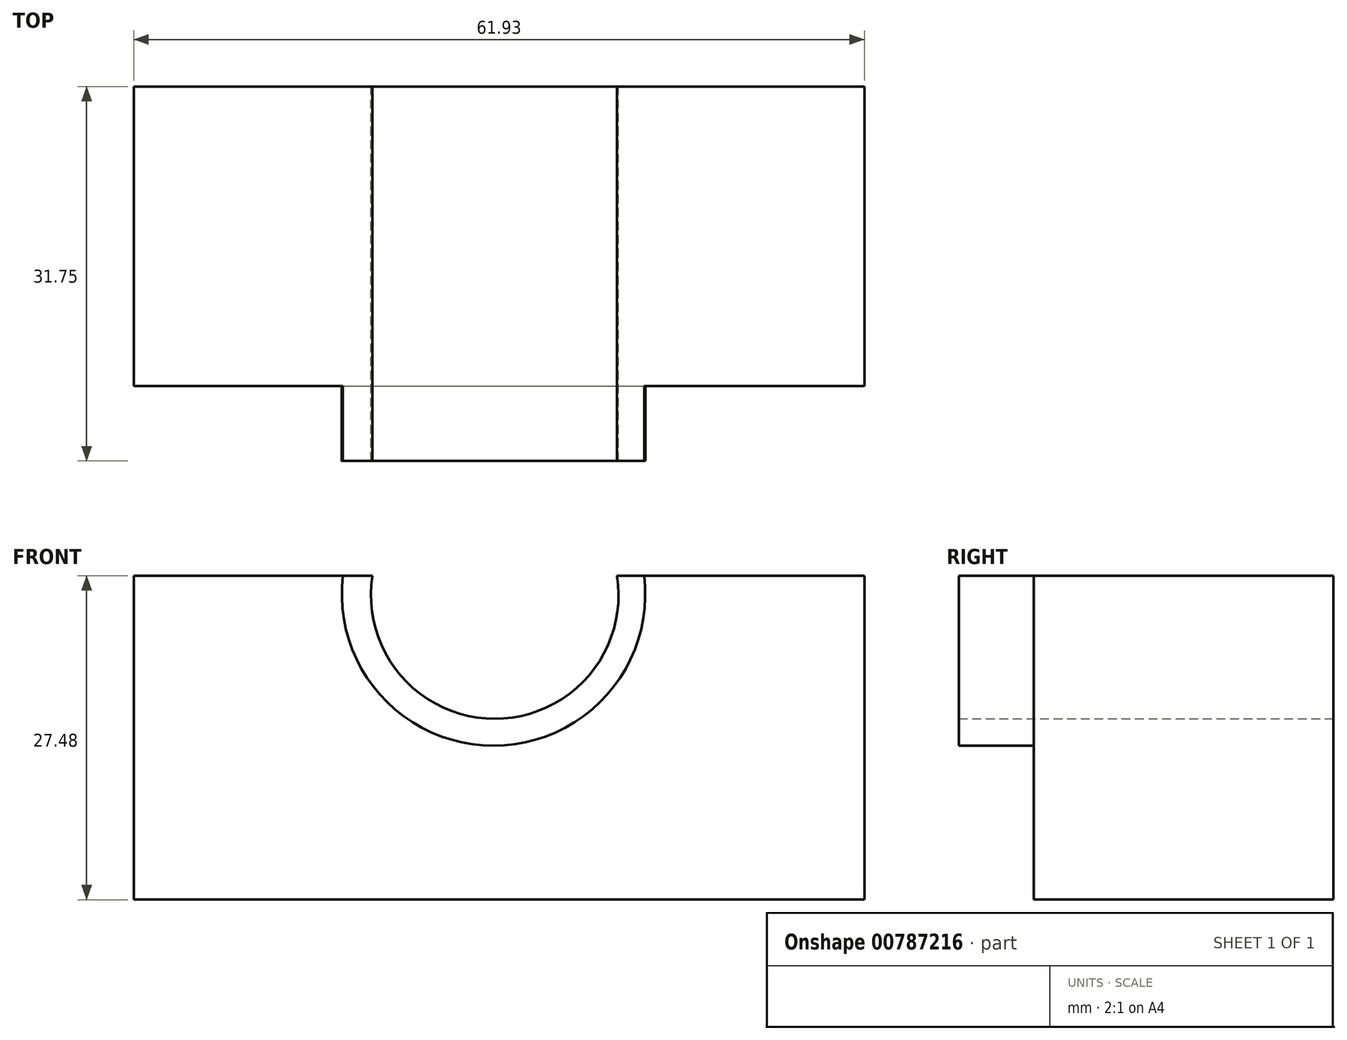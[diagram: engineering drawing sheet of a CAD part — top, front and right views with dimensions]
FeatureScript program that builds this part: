
annotation { "Feature Type Name" : "Feature", "Feature Type Description" : "" }
export const myFeature = defineFeature(function(context is Context, id is Id, definition is map)
    precondition{}
    {
        {
            var Q0;
            Q0=qCreatedBy(makeId("Front.planeOp"),FACE);
            var sketch = newSketch(context, id + "F0", { "sketchPlane" : qUnion([Q0])});
            skLineSegment(sketch, "E0.bottom", {"start": v(-25.42, -10.97) * mm, "end": v(36.51, -10.97) * mm});
            skLineSegment(sketch, "E0.left", {"start": v(-25.42, -10.97) * mm, "end": v(-25.42, 16.5) * mm});
            skLineSegment(sketch, "E0.right", {"start": v(36.51, -10.97) * mm, "end": v(36.51, 16.5) * mm});
            skLineSegment(sketch, "E1", {"start": v(-25.42, 16.5) * mm, "end": v(-8.31, 16.5) * mm});
            skLineSegment(sketch, "E2", {"start": v(36.51, 16.5) * mm, "end": v(19.16, 16.5) * mm});
            skArc(sketch, "E3", {"start": v(-8.31, 16.5) * mm, "mid": v(5.42, 0.84) * mm, "end": v(19.16, 16.5) * mm});
            skLineSegment(sketch, "E4", {"start": v(-8.31, 16.5) * mm, "end": v(-5.18, 16.5) * mm});
            skLineSegment(sketch, "E5", {"start": v(19.16, 16.5) * mm, "end": v(15.54, 16.5) * mm});
            skArc(sketch, "E6", {"start": v(-5.18, 16.5) * mm, "mid": v(5.18, 4.38) * mm, "end": v(15.54, 16.5) * mm});
            skSolve(sketch);
        }
        {
            var Q0;
            Q0 = qSketchRegion(id + "F0", true);
            extrude(context, id + "F1", {"entities" : qUnion([Q0]), "depth" : 25.4 * mm, "offsetDistance" : 25.4 * mm});
        }
        {
            var Q0;
            Q0=makeQuery(id+"F1.opExtrude","SWEPT_FACE",FACE,{"disambiguationData":[OSD([sQuery(id+"F0.wireOp",EDGE,"E1"),sQuery(id+"F0.wireOp",EDGE,"E4")])]});
            var sketch = newSketch(context, id + "F2", { "sketchPlane" : qUnion([Q0])});
            skCircle(sketch, "E7", {"center": v(26.73, -12.85) * mm, "radius": 3.02 * mm});
            skCircle(sketch, "E8", {"center": v(-15.83, -12.42) * mm, "radius": 3.02 * mm});
            skSolve(sketch);
        }
        {
            var Q0;
            Q0=makeQuery(id+"F2.imprint","IMPRINT",FACE,{"disambiguationData":[TD([[makeQuery(id+"F2.imprint","IMPRINT",EDGE,{"derivedFrom":sQuery(id+"F2.wireOp",EDGE,"E8")}),1.0]])]});
            extrude(context, id + "F3", {"entities" : qUnion([Q0]), "operationType" : NewBodyOperationType.ADD, "depth" : -25.4 * mm, "offsetDistance" : 25.4 * mm});
        }
        {
            var Q0;
            Q0=makeQuery(id+"F1.opExtrude","CAP_FACE",FACE,{"disambiguationData":[OSD([sQuery(id+"F0.wireOp",EDGE,"E0.bottom"),sQuery(id+"F0.wireOp",EDGE,"E0.left"),sQuery(id+"F0.wireOp",EDGE,"E0.right"),sQuery(id+"F0.wireOp",EDGE,"E1"),sQuery(id+"F0.wireOp",EDGE,"E2"),sQuery(id+"F0.wireOp",EDGE,"E4"),sQuery(id+"F0.wireOp",EDGE,"E5"),sQuery(id+"F0.wireOp",EDGE,"E6")])],"isStart":false});
            var sketch = newSketch(context, id + "F4", { "sketchPlane" : qUnion([Q0])});
            skCircle(sketch, "E9", {"center": v(25.9, -12.65) * mm, "radius": 3.62 * mm});
            skArc(sketch, "E10", {"start": v(-7.69, 16.5) * mm, "mid": v(5.08, 2.1) * mm, "end": v(17.84, 16.5) * mm});
            skSolve(sketch);
        }
        {
            var Q0;
            {var subQ0=sQuery(id+"F4.wireOp",EDGE,"E10");Q0=makeQuery(id+"F4.imprint","IMPRINT",FACE,{"disambiguationData":[TD([[makeQuery(id+"F4.imprint","IMPRINT",EDGE,{"derivedFrom":subQ0}),1.0]])]});}
            extrude(context, id + "F5", {"entities" : qUnion([Q0]), "operationType" : NewBodyOperationType.ADD, "depth" : 6.35 * mm, "offsetDistance" : 25.4 * mm});
        }
    });
